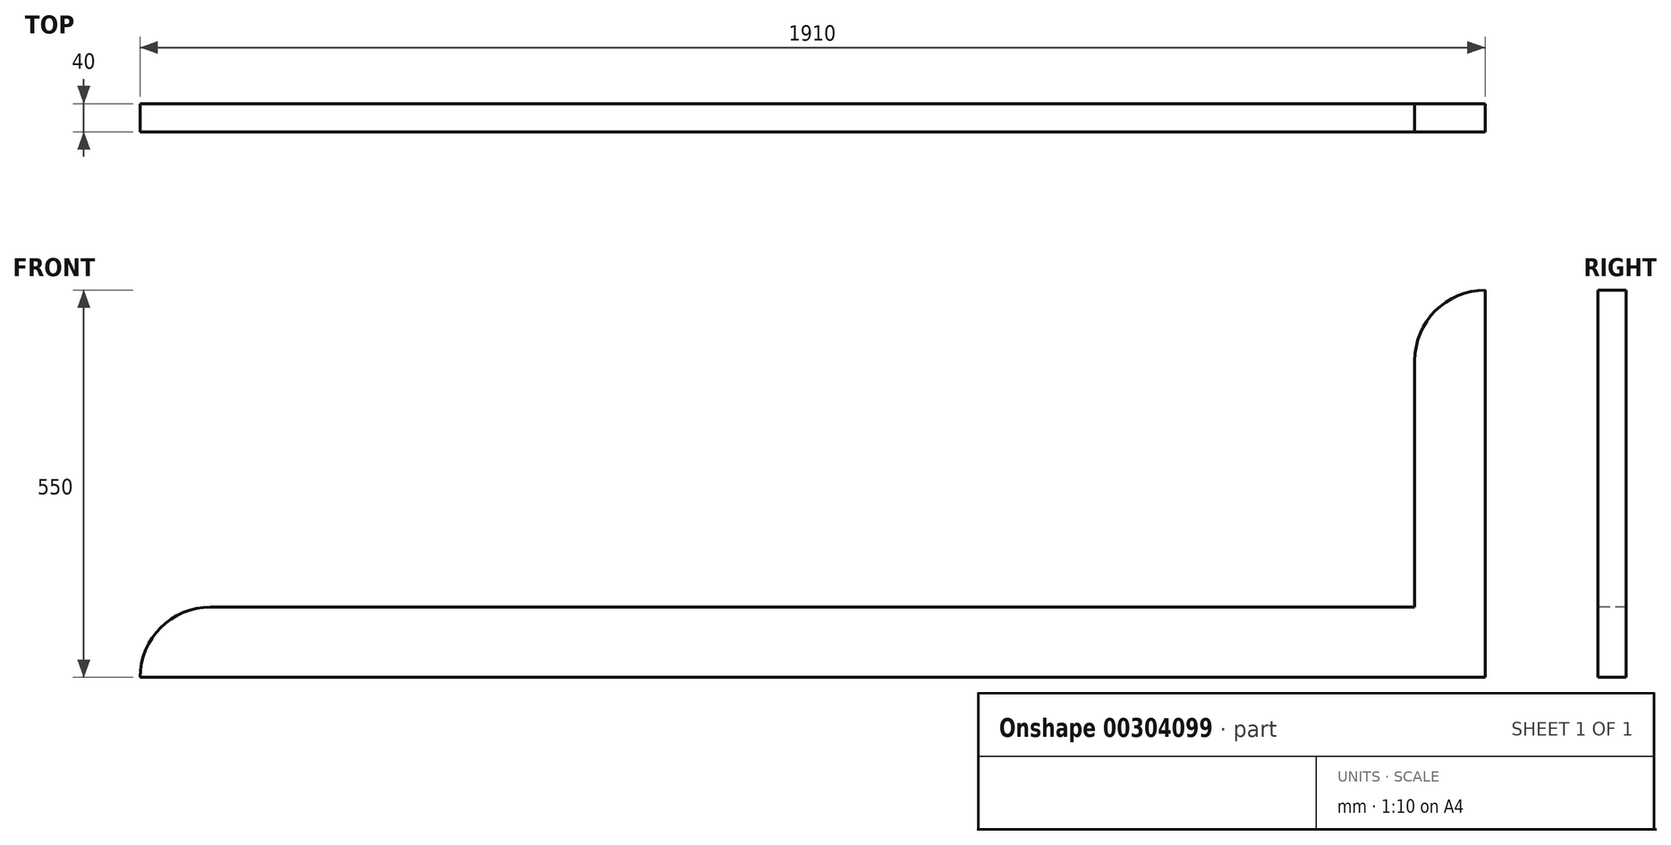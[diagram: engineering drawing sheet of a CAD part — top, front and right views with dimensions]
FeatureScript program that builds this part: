
annotation { "Feature Type Name" : "Feature", "Feature Type Description" : "" }
export const myFeature = defineFeature(function(context is Context, id is Id, definition is map)
    precondition{}
    {
        {
            var Q0;
            Q0=qCreatedBy(makeId("Top.planeOp"),FACE);
            var sketch = newSketch(context, id + "F0", { "sketchPlane" : qUnion([Q0])});
            skLineSegment(sketch, "E0.bottom", {"start": v(-944.47, -92.94) * mm, "end": v(965.53, -92.94) * mm});
            skLineSegment(sketch, "E0.top", {"start": v(-944.47, -132.94) * mm, "end": v(965.53, -132.94) * mm});
            skLineSegment(sketch, "E0.left", {"start": v(-944.47, -92.94) * mm, "end": v(-944.47, -132.94) * mm});
            skLineSegment(sketch, "E0.right", {"start": v(965.53, -92.94) * mm, "end": v(965.53, -132.94) * mm});
            skSolve(sketch);
        }
        {
            var Q0;
            Q0=makeQuery(id+"F0.imprint","IMPRINT",FACE,{"disambiguationData":[TD([[makeQuery(id+"F0.imprint","IMPRINT",EDGE,{"derivedFrom":sQuery(id+"F0.wireOp",EDGE,"E0.bottom")}),-1.0]])]});
            extrude(context, id + "F1", {"entities" : qUnion([Q0]), "depth" : 100 * mm, "offsetDistance" : 25 * mm});
        }
        {
            var Q0;
            Q0=makeQuery(id+"F1.opExtrude","CAP_FACE",FACE,{"disambiguationData":[OSD([sQuery(id+"F0.wireOp",EDGE,"E0.bottom"),sQuery(id+"F0.wireOp",EDGE,"E0.top"),sQuery(id+"F0.wireOp",EDGE,"E0.left"),sQuery(id+"F0.wireOp",EDGE,"E0.right")])],"isStart":false});
            var sketch = newSketch(context, id + "F2", { "sketchPlane" : qUnion([Q0])});
            skLineSegment(sketch, "E1.bottom", {"start": v(965.53, -132.94) * mm, "end": v(865.53, -132.94) * mm});
            skLineSegment(sketch, "E1.top", {"start": v(965.53, -92.94) * mm, "end": v(865.53, -92.94) * mm});
            skLineSegment(sketch, "E1.left", {"start": v(965.53, -132.94) * mm, "end": v(965.53, -92.94) * mm});
            skLineSegment(sketch, "E1.right", {"start": v(865.53, -132.94) * mm, "end": v(865.53, -92.94) * mm});
            skSolve(sketch);
        }
        {
            var Q0;
            Q0=makeQuery(id+"F2.imprint","IMPRINT",FACE,{"disambiguationData":[TD([[makeQuery(id+"F2.imprint","IMPRINT",EDGE,{"derivedFrom":sQuery(id+"F2.wireOp",EDGE,"E1.bottom")}),1.0]])]});
            extrude(context, id + "F3", {"entities" : qUnion([Q0]), "operationType" : NewBodyOperationType.ADD, "depth" : 450 * mm, "offsetDistance" : 25 * mm});
        }
        {
            var Q0;
            Q0=makeQuery(id+"F1.opExtrude","CAP_EDGE",EDGE,{"disambiguationData":[OSD([sQuery(id+"F0.wireOp",EDGE,"E0.left")])],"isStart":false});
            var Q1;
            Q1=makeQuery(id+"F3.opExtrude","CAP_EDGE",EDGE,{"disambiguationData":[OSD([sQuery(id+"F2.wireOp",EDGE,"E1.right")])],"isStart":false});
            fillet(context, id + "F4", {"entities" : qUnion([Q0, Q1]), "radius" : 100 * mm, "tangentPropagation" : true, "allowEdgeOverflow" : false});
        }
    });
